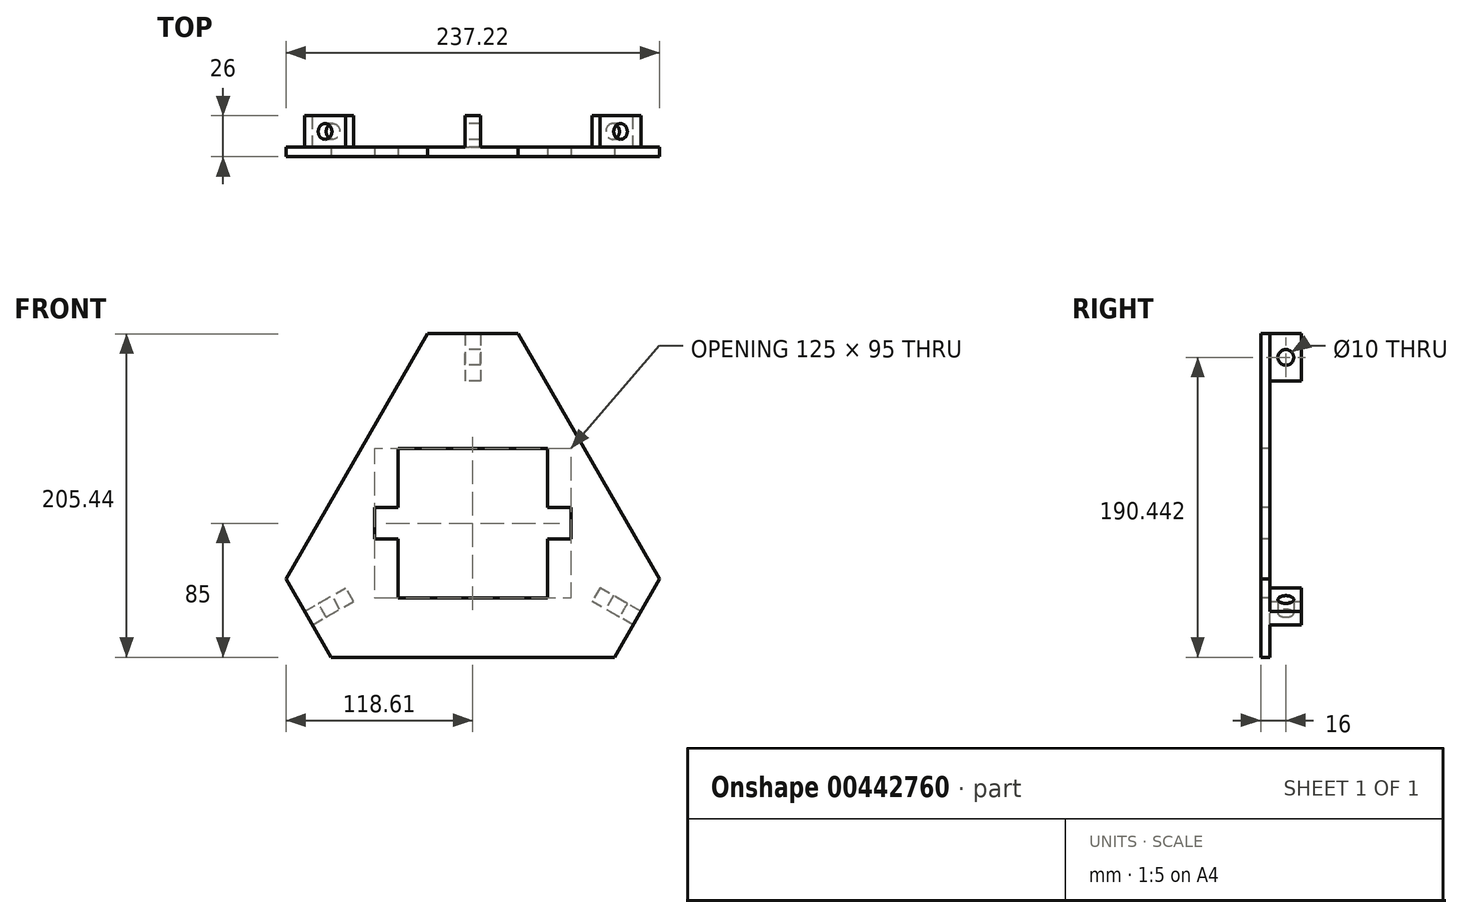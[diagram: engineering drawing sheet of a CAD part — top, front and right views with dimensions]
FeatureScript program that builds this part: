
annotation { "Feature Type Name" : "Feature", "Feature Type Description" : "" }
export const myFeature = defineFeature(function(context is Context, id is Id, definition is map)
    precondition{}
    {
        {
            var Q0;
            Q0=qCreatedBy(makeId("Front.planeOp"),FACE);
            var sketch = newSketch(context, id + "F0", { "sketchPlane" : qUnion([Q0])});
            skLineSegment(sketch, "E0", {"start": v(-28.61, 205.44) * mm, "end": v(-118.61, 49.56) * mm});
            skLineSegment(sketch, "E1", {"start": v(-118.61, 49.56) * mm, "end": v(-90, 0) * mm});
            skLineSegment(sketch, "E2", {"start": v(-90, 0) * mm, "end": v(90, 0) * mm});
            skLineSegment(sketch, "E3", {"start": v(90, 0) * mm, "end": v(118.61, 49.56) * mm});
            skLineSegment(sketch, "E4", {"start": v(118.61, 49.56) * mm, "end": v(28.61, 205.44) * mm});
            skLineSegment(sketch, "E5", {"start": v(28.61, 205.44) * mm, "end": v(-28.61, 205.44) * mm});
            skLineSegment(sketch, "E6", {"start": v(-104.3, 24.78) * mm, "end": v(73.61, 127.5) * mm, "construction": true});
            skLineSegment(sketch, "E7", {"start": v(104.3, 24.78) * mm, "end": v(-73.61, 127.5) * mm, "construction": true});
            skLineSegment(sketch, "E8", {"start": v(0, 205.44) * mm, "end": v(0, 0) * mm, "construction": true});
            skSolve(sketch);
        }
        {
            var Q0;
            Q0 = qSketchRegion(id + "F0", true);
            extrude(context, id + "F1", {"entities" : qUnion([Q0]), "oppositeDirection" : true, "depth" : 6 * mm});
        }
        {
            var Q0;
            Q0=qCreatedBy(makeId("Front.planeOp"),FACE);
            var sketch = newSketch(context, id + "F2", { "sketchPlane" : qUnion([Q0])});
            skLineSegment(sketch, "E9", {"start": v(-47.5, 132.5) * mm, "end": v(47.5, 132.5) * mm});
            skLineSegment(sketch, "E10", {"start": v(47.5, 132.5) * mm, "end": v(47.5, 95) * mm});
            skLineSegment(sketch, "E11", {"start": v(47.5, 95) * mm, "end": v(62.5, 95) * mm});
            skLineSegment(sketch, "E12", {"start": v(62.5, 95) * mm, "end": v(62.5, 75) * mm});
            skLineSegment(sketch, "E13", {"start": v(62.5, 75) * mm, "end": v(47.5, 75) * mm});
            skLineSegment(sketch, "E14", {"start": v(47.5, 75) * mm, "end": v(47.5, 37.5) * mm});
            skLineSegment(sketch, "E15", {"start": v(47.5, 37.5) * mm, "end": v(-47.5, 37.5) * mm});
            skLineSegment(sketch, "E16", {"start": v(-47.5, 37.5) * mm, "end": v(-47.5, 75) * mm});
            skLineSegment(sketch, "E17", {"start": v(-47.5, 75) * mm, "end": v(-62.5, 75) * mm});
            skLineSegment(sketch, "E18", {"start": v(-62.5, 75) * mm, "end": v(-62.5, 95) * mm});
            skLineSegment(sketch, "E19", {"start": v(-62.5, 95) * mm, "end": v(-47.5, 95) * mm});
            skLineSegment(sketch, "E20", {"start": v(-47.5, 95) * mm, "end": v(-47.5, 132.5) * mm});
            skSolve(sketch);
        }
        {
            var Q0;
            Q0 = qSketchRegion(id + "F2", true);
            extrude(context, id + "F3", {"entities" : qUnion([Q0]), "operationType" : NewBodyOperationType.REMOVE, "oppositeDirection" : true, "depth" : 25 * mm});
        }
        {
            var Q0;
            Q0=qCreatedBy(makeId("Right.planeOp"),FACE);
            var sketch = newSketch(context, id + "F4", { "sketchPlane" : qUnion([Q0])});
            skLineSegment(sketch, "E21.bottom", {"start": v(6, 205.44) * mm, "end": v(26, 205.44) * mm});
            skLineSegment(sketch, "E21.top", {"start": v(6, 175.44) * mm, "end": v(26, 175.44) * mm});
            skLineSegment(sketch, "E21.left", {"start": v(6, 205.44) * mm, "end": v(6, 175.44) * mm});
            skLineSegment(sketch, "E21.right", {"start": v(26, 205.44) * mm, "end": v(26, 175.44) * mm});
            skCircle(sketch, "E22", {"center": v(16, 190.44) * mm, "radius": 5 * mm});
            skPoint(sketch, "E22.centerSnap0", {"position": v(16, 205.44) * mm});
            skPoint(sketch, "E22.centerSnap1", {"position": v(26, 190.44) * mm});
            skSolve(sketch);
        }
        {
            var Q0;
            Q0 = qSketchRegion(id + "F4", true);
            extrude(context, id + "F5", {"entities" : qUnion([Q0]), "operationType" : NewBodyOperationType.ADD, "depth" : 5 * mm, "hasSecondDirection" : true, "secondDirectionOppositeDirection" : true, "secondDirectionDepth" : 5 * mm});
        }
        {
            var Q0;
            Q0=makeQuery(id+"F1.opExtrude","CAP_EDGE",EDGE,{"disambiguationData":[OSD([sQuery(id+"F0.wireOp",EDGE,"E3")])],"isStart":false});
            cPoint(context, id + "F6", {"entities" : qUnion([Q0]), "parameter" : 0.5});
        }
        {
            var Q0;
            Q0=makeQuery(id+"F1.opExtrude","CAP_EDGE",EDGE,{"disambiguationData":[OSD([sQuery(id+"F0.wireOp",EDGE,"E3")])],"isStart":true});
            cPoint(context, id + "F7", {"entities" : qUnion([Q0]), "parameter" : 0.5});
        }
        {
            var Q0;
            Q0=makeQuery(id+"F1.opExtrude","CAP_EDGE",EDGE,{"disambiguationData":[OSD([sQuery(id+"F0.wireOp",EDGE,"E0")])],"isStart":false});
            cPoint(context, id + "F8", {"entities" : qUnion([Q0]), "parameter" : 0.5});
        }
        {
            var Q0;
            Q0 = qCreatedBy(id + "F6" ,VERTEX);
            var Q1;
            Q1 = qCreatedBy(id + "F7" ,VERTEX);
            var Q2;
            Q2 = qCreatedBy(id + "F8" ,VERTEX);
            cPlane(context, id + "F9", {"entities" : qUnion([Q0, Q1, Q2]), "cplaneType" : CPlaneType.THREE_POINT, "offset" : 25 * mm, "width" : 150 * mm, "height" : 150 * mm});
        }
        {
            var Q0;
            Q0=qCreatedBy(id+"F9.planeOp",FACE);
            var sketch = newSketch(context, id + "F10", { "sketchPlane" : qUnion([Q0])});
            skLineSegment(sketch, "E23.bottom", {"start": v(77.94, 6) * mm, "end": v(47.94, 6) * mm});
            skLineSegment(sketch, "E23.top", {"start": v(77.94, 26) * mm, "end": v(47.94, 26) * mm});
            skLineSegment(sketch, "E23.left", {"start": v(77.94, 6) * mm, "end": v(77.94, 26) * mm});
            skLineSegment(sketch, "E23.right", {"start": v(47.94, 6) * mm, "end": v(47.94, 26) * mm});
            skCircle(sketch, "E24", {"center": v(62.94, 16) * mm, "radius": 5 * mm});
            skPoint(sketch, "E24.centerSnap0", {"position": v(77.94, 16) * mm});
            skPoint(sketch, "E24.centerSnap1", {"position": v(62.94, 26) * mm});
            skSolve(sketch);
        }
        {
            var Q0;
            Q0 = qSketchRegion(id + "F10", true);
            extrude(context, id + "F11", {"entities" : qUnion([Q0]), "operationType" : NewBodyOperationType.ADD, "depth" : 5 * mm, "hasSecondDirection" : true, "secondDirectionOppositeDirection" : true, "secondDirectionDepth" : 5 * mm});
        }
        {
            var Q0;
            Q0=makeQuery(id+"F1.opExtrude","CAP_EDGE",EDGE,{"disambiguationData":[OSD([sQuery(id+"F0.wireOp",EDGE,"E1")])],"isStart":false});
            cPoint(context, id + "F12", {"entities" : qUnion([Q0]), "parameter" : 0.5});
        }
        {
            var Q0;
            Q0=makeQuery(id+"F1.opExtrude","CAP_EDGE",EDGE,{"disambiguationData":[OSD([sQuery(id+"F0.wireOp",EDGE,"E1")])],"isStart":true});
            cPoint(context, id + "F13", {"entities" : qUnion([Q0]), "parameter" : 0.5});
        }
        {
            var Q0;
            Q0=makeQuery(id+"F1.opExtrude","CAP_EDGE",EDGE,{"disambiguationData":[OSD([sQuery(id+"F0.wireOp",EDGE,"E4")])],"isStart":false});
            cPoint(context, id + "F14", {"entities" : qUnion([Q0]), "parameter" : 0.5});
        }
        {
            var Q0;
            Q0 = qCreatedBy(id + "F12" ,VERTEX);
            var Q1;
            Q1 = qCreatedBy(id + "F13" ,VERTEX);
            var Q2;
            Q2 = qCreatedBy(id + "F14" ,VERTEX);
            cPlane(context, id + "F15", {"entities" : qUnion([Q0, Q1, Q2]), "cplaneType" : CPlaneType.THREE_POINT, "offset" : 25 * mm, "width" : 150 * mm, "height" : 150 * mm});
        }
        {
            var Q0;
            Q0=qCreatedBy(id+"F15.planeOp",FACE);
            var sketch = newSketch(context, id + "F16", { "sketchPlane" : qUnion([Q0])});
            skLineSegment(sketch, "E25.bottom", {"start": v(-77.94, -6) * mm, "end": v(-47.94, -6) * mm});
            skLineSegment(sketch, "E25.top", {"start": v(-77.94, -26) * mm, "end": v(-47.94, -26) * mm});
            skLineSegment(sketch, "E25.left", {"start": v(-77.94, -6) * mm, "end": v(-77.94, -26) * mm});
            skLineSegment(sketch, "E25.right", {"start": v(-47.94, -6) * mm, "end": v(-47.94, -26) * mm});
            skCircle(sketch, "E26", {"center": v(-62.94, -16) * mm, "radius": 5 * mm});
            skPoint(sketch, "E26.centerSnap0", {"position": v(-77.94, -16) * mm});
            skPoint(sketch, "E26.centerSnap1", {"position": v(-62.94, -6) * mm});
            skSolve(sketch);
        }
        {
            var Q0;
            Q0 = qSketchRegion(id + "F16", true);
            extrude(context, id + "F17", {"entities" : qUnion([Q0]), "operationType" : NewBodyOperationType.ADD, "depth" : 5 * mm, "hasSecondDirection" : true, "secondDirectionOppositeDirection" : true, "secondDirectionDepth" : 5 * mm});
        }
    });
